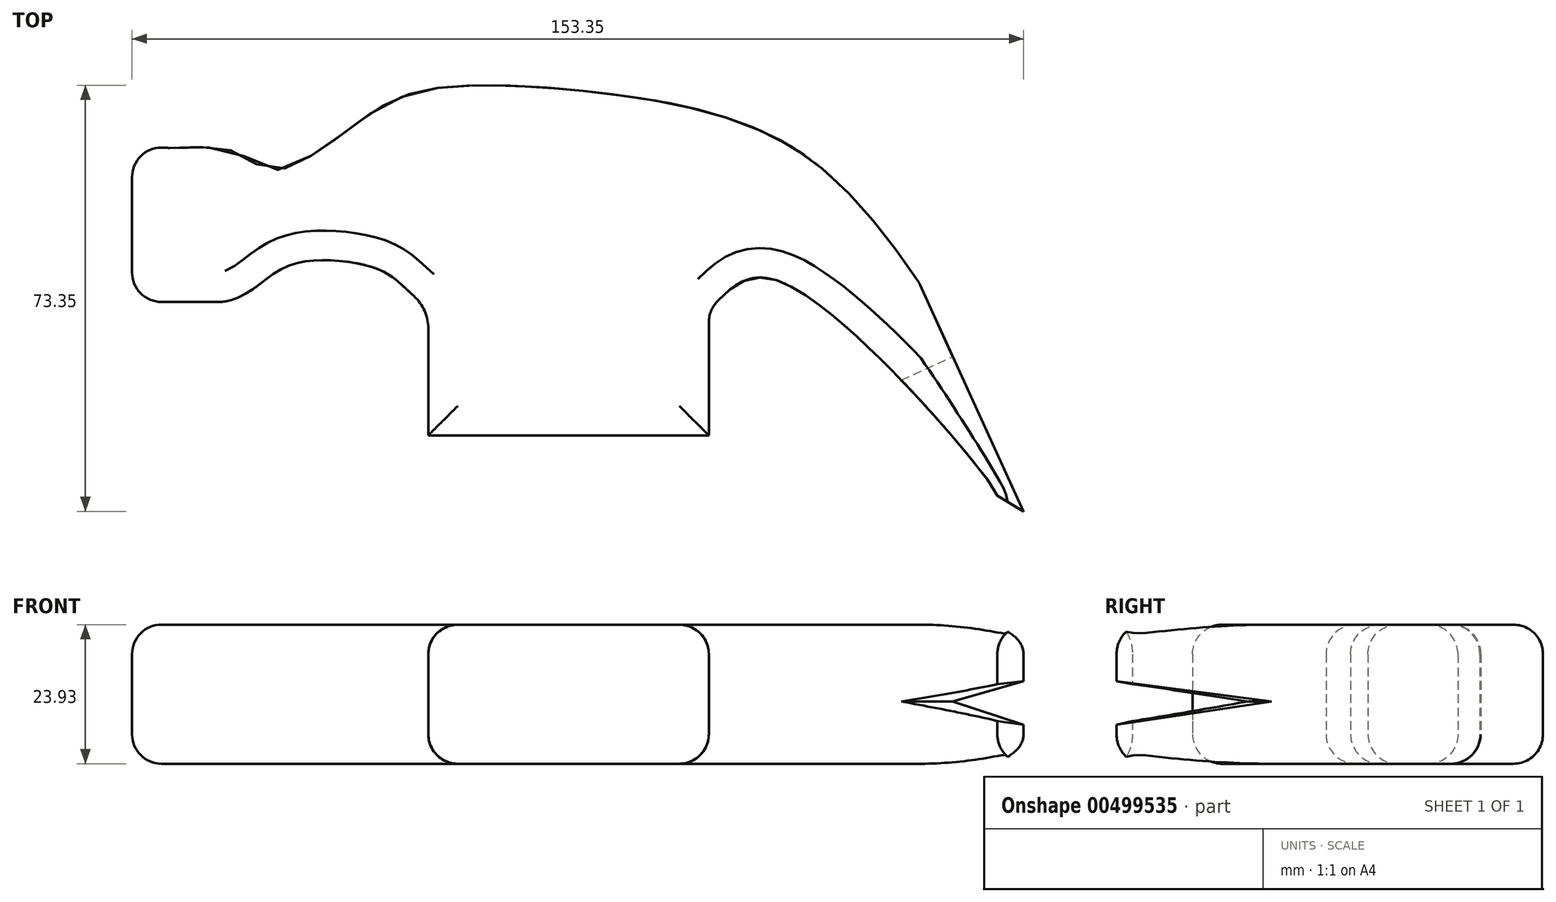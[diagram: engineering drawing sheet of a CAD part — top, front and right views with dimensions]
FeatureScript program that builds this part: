
annotation { "Feature Type Name" : "Feature", "Feature Type Description" : "" }
export const myFeature = defineFeature(function(context is Context, id is Id, definition is map)
    precondition{}
    {
        {
            var Q0;
            Q0=qCreatedBy(makeId("Top.planeOp"),FACE);
            var sketch = newSketch(context, id + "F0", { "sketchPlane" : qUnion([Q0])});
            skLineSegment(sketch, "E0", {"start": v(-10.61, 0) * mm, "end": v(37.65, 0) * mm});
            skLineSegment(sketch, "E1", {"start": v(37.65, 0) * mm, "end": v(37.65, 21.77) * mm});
            skLineSegment(sketch, "E2", {"start": v(-10.61, 0) * mm, "end": v(-10.61, 21.77) * mm});
            skFitSpline(sketch, "E3", {"points": [v(37.65, 21.77) * mm, v(44.7, 26.45) * mm, v(54.36, 21.77) * mm, v(79.22, -6.3) * mm, v(79.22, -6.6) * mm], "startDerivative": vector(30.13, 27.36) * mm, "endDerivative": vector(-2.7, -3.94) * mm});
            skLineSegment(sketch, "E4", {"start": v(79.26, -6.54) * mm, "end": v(79.08, -6.04) * mm});
            skPoint(sketch, "E5.2.internal.orphan", {"position": v(-19.94, 20.6) * mm});
            skPoint(sketch, "E5.3.internal.orphan", {"position": v(-16.43, 20.6) * mm});
            skPoint(sketch, "E6.end.orphan", {"position": v(-42.75, 20.6) * mm});
            skFitSpline(sketch, "E7", {"points": [v(37.65, 21.77) * mm, v(39.92, 23.84) * mm, v(49.94, 26.45) * mm, v(87.26, -10.36) * mm, v(86.36, -10.06) * mm], "startDerivative": vector(14.67, 12.53) * mm, "endDerivative": vector(-18.32, 11.04) * mm});
            skLineSegment(sketch, "E8", {"start": v(87.26, -10.36) * mm, "end": v(91.78, -13.07) * mm});
            skLineSegment(sketch, "E9", {"start": v(91.78, -13.07) * mm, "end": v(73.72, 26.45) * mm});
            skFitSpline(sketch, "E10", {"points": [v(73.72, 26.45) * mm, v(52.65, 49.23) * mm, v(17.14, 59.16) * mm, v(-12.35, 59.16) * mm, v(-24.1, 52.84) * mm, v(-37.3, 45.66) * mm, v(-45.16, 49.23) * mm, v(-55.25, 49.53) * mm], "startDerivative": vector(-91.6, 130.06) * mm, "endDerivative": vector(6.83, 13.17) * mm});
            skLineSegment(sketch, "E11", {"start": v(-55.25, 49.53) * mm, "end": v(-61.57, 49.53) * mm});
            skLineSegment(sketch, "E12", {"start": v(-61.57, 49.53) * mm, "end": v(-61.57, 22.98) * mm});
            skLineSegment(sketch, "E13", {"start": v(-61.57, 22.98) * mm, "end": v(-45.16, 22.98) * mm});
            skFitSpline(sketch, "E14", {"points": [v(-45.16, 22.98) * mm, v(-34.24, 29.38) * mm, v(-19.84, 28.83) * mm, v(-10.61, 21.77) * mm], "startDerivative": vector(49.9, 17.9) * mm, "endDerivative": vector(46.44, -40.57) * mm});
            skSolve(sketch);
        }
        {
            var Q0;
            Q0=makeQuery(id+"F0.imprint","IMPRINT",FACE,{"disambiguationData":[TD([[makeQuery(id+"F0.imprint","IMPRINT",EDGE,{"derivedFrom":sQuery(id+"F0.wireOp",EDGE,"E0")}),1.0]])]});
            extrude(context, id + "F1", {"entities" : qUnion([Q0]), "depth" : 23.93 * mm});
        }
        {
            var Q0;
            Q0=makeQuery(id+"F1.opExtrude","SWEPT_EDGE",EDGE,{"disambiguationData":[OSD([sQuery(id+"F0.wireOp",EDGE,"E9"),sQuery(id+"F0.wireOp",EDGE,"E10")])]});
            fillet(context, id + "F2", {"entities" : qUnion([Q0]), "radius" : 5.08 * mm, "tangentPropagation" : true, "allowEdgeOverflow" : false});
        }
        {
            var Q0;
            Q0=makeQuery(id+"F1.opExtrude","SWEPT_EDGE",EDGE,{"disambiguationData":[OSD([sQuery(id+"F0.wireOp",EDGE,"E1"),sQuery(id+"F0.wireOp",EDGE,"E7")])]});
            fillet(context, id + "F3", {"entities" : qUnion([Q0]), "radius" : 5.08 * mm, "tangentPropagation" : true, "allowEdgeOverflow" : false});
        }
        {
            var Q0;
            Q0=makeQuery(id+"F1.opExtrude","SWEPT_EDGE",EDGE,{"disambiguationData":[OSD([sQuery(id+"F0.wireOp",EDGE,"E2"),sQuery(id+"F0.wireOp",EDGE,"E14")])]});
            fillet(context, id + "F4", {"entities" : qUnion([Q0]), "radius" : 7.62 * mm, "tangentPropagation" : true, "allowEdgeOverflow" : false});
        }
        {
            var Q0;
            Q0=makeQuery(id+"F1.opExtrude","SWEPT_EDGE",EDGE,{"disambiguationData":[OSD([sQuery(id+"F0.wireOp",EDGE,"E13"),sQuery(id+"F0.wireOp",EDGE,"E14")])]});
            fillet(context, id + "F5", {"entities" : qUnion([Q0]), "radius" : 7.62 * mm, "tangentPropagation" : true, "allowEdgeOverflow" : false});
        }
        {
            var Q0;
            Q0=makeQuery(id+"F1.opExtrude","SWEPT_FACE",FACE,{"disambiguationData":[OSD([sQuery(id+"F0.wireOp",EDGE,"E9")])]});
            var sketch = newSketch(context, id + "F6", { "sketchPlane" : qUnion([Q0])});
            skLineSegment(sketch, "E15", {"start": v(-50.03, 6.74) * mm, "end": v(-20.74, 10.72) * mm});
            skLineSegment(sketch, "E16", {"start": v(-20.74, 10.72) * mm, "end": v(-50.03, 14.2) * mm});
            skLineSegment(sketch, "E17", {"start": v(-50.03, 14.2) * mm, "end": v(-50.03, 6.74) * mm});
            skSolve(sketch);
        }
        {
            var Q0;
            Q0 = qSketchRegion(id + "F6", true);
            extrude(context, id + "F7", {"entities" : qUnion([Q0]), "operationType" : NewBodyOperationType.REMOVE, "oppositeDirection" : true, "depth" : 25.4 * mm, "offsetDistance" : 25.4 * mm});
        }
        {
            var Q0;
            Q0=makeQuery(id+"F1.opExtrude","CAP_FACE",FACE,{"disambiguationData":[OSD([sQuery(id+"F0.wireOp",EDGE,"E0"),sQuery(id+"F0.wireOp",EDGE,"E1"),sQuery(id+"F0.wireOp",EDGE,"E2"),sQuery(id+"F0.wireOp",EDGE,"E7"),sQuery(id+"F0.wireOp",EDGE,"E8"),sQuery(id+"F0.wireOp",EDGE,"E9"),sQuery(id+"F0.wireOp",EDGE,"E10"),sQuery(id+"F0.wireOp",EDGE,"E11"),sQuery(id+"F0.wireOp",EDGE,"E12"),sQuery(id+"F0.wireOp",EDGE,"E13"),sQuery(id+"F0.wireOp",EDGE,"E14")])],"isStart":false});
            var Q1;
            Q1=makeQuery(id+"F1.opExtrude","SWEPT_FACE",FACE,{"disambiguationData":[OSD([sQuery(id+"F0.wireOp",EDGE,"E10")])]});
            var Q2;
            Q2=makeQuery(id+"F1.opExtrude","CAP_FACE",FACE,{"disambiguationData":[OSD([sQuery(id+"F0.wireOp",EDGE,"E0"),sQuery(id+"F0.wireOp",EDGE,"E1"),sQuery(id+"F0.wireOp",EDGE,"E2"),sQuery(id+"F0.wireOp",EDGE,"E7"),sQuery(id+"F0.wireOp",EDGE,"E8"),sQuery(id+"F0.wireOp",EDGE,"E9"),sQuery(id+"F0.wireOp",EDGE,"E10"),sQuery(id+"F0.wireOp",EDGE,"E11"),sQuery(id+"F0.wireOp",EDGE,"E12"),sQuery(id+"F0.wireOp",EDGE,"E13"),sQuery(id+"F0.wireOp",EDGE,"E14")])],"isStart":true});
            var Q3;
            Q3=makeQuery(id+"F1.opExtrude","SWEPT_FACE",FACE,{"disambiguationData":[OSD([sQuery(id+"F0.wireOp",EDGE,"E12")])]});
            fillet(context, id + "F8", {"entities" : qUnion([Q0, Q1, Q2, Q3]), "radius" : 5.08 * mm, "tangentPropagation" : true, "allowEdgeOverflow" : false});
        }
    });
